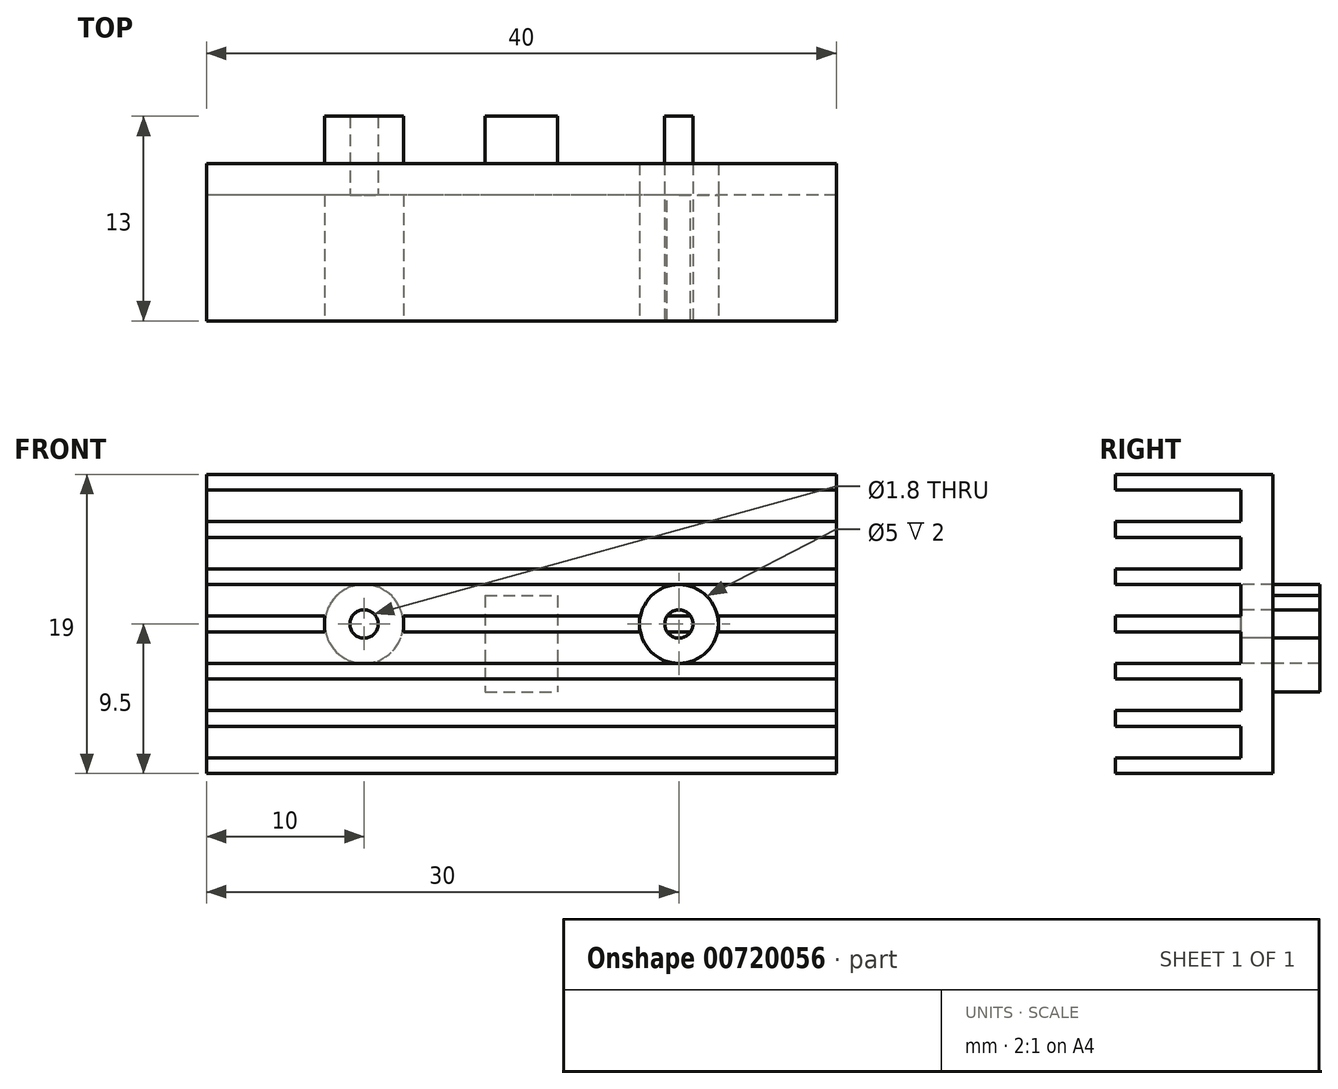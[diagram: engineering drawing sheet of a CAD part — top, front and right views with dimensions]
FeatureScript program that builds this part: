
annotation { "Feature Type Name" : "Feature", "Feature Type Description" : "" }
export const myFeature = defineFeature(function(context is Context, id is Id, definition is map)
    precondition{}
    {
        {
            var Q0;
            Q0=qCreatedBy(makeId("Front.planeOp"),FACE);
            var sketch = newSketch(context, id + "F0", { "sketchPlane" : qUnion([Q0])});
            skLineSegment(sketch, "E0", {"start": v(0, 0) * mm, "end": v(-20, 0) * mm, "construction": true});
            skLineSegment(sketch, "E1", {"start": v(-20, 0) * mm, "end": v(-20, 9.5) * mm, "construction": true});
            skLineSegment(sketch, "E2.bottom", {"start": v(-20, 9.5) * mm, "end": v(20, 9.5) * mm});
            skLineSegment(sketch, "E2.top", {"start": v(-20, -9.5) * mm, "end": v(20, -9.5) * mm});
            skLineSegment(sketch, "E2.left", {"start": v(-20, 9.5) * mm, "end": v(-20, -9.5) * mm});
            skLineSegment(sketch, "E2.right", {"start": v(20, 9.5) * mm, "end": v(20, -9.5) * mm});
            skPoint(sketch, "E2.middle", {"position": v(0, 0) * mm});
            skSolve(sketch);
        }
        {
            var Q0;
            Q0=makeQuery(id+"F0.imprint","IMPRINT",FACE,{"disambiguationData":[TD([[makeQuery(id+"F0.imprint","IMPRINT",EDGE,{"derivedFrom":sQuery(id+"F0.wireOp",EDGE,"E2.bottom")}),-1.0]])]});
            extrude(context, id + "F1", {"entities" : qUnion([Q0]), "depth" : 10 * mm, "offsetDistance" : 25 * mm});
        }
        {
            var Q0;
            Q0=makeQuery(id+"F1.opExtrude","CAP_FACE",FACE,{"disambiguationData":[OSD([sQuery(id+"F0.wireOp",EDGE,"E2.bottom"),sQuery(id+"F0.wireOp",EDGE,"E2.top"),sQuery(id+"F0.wireOp",EDGE,"E2.left"),sQuery(id+"F0.wireOp",EDGE,"E2.right")])],"isStart":false});
            var sketch = newSketch(context, id + "F2", { "sketchPlane" : qUnion([Q0])});
            skLineSegment(sketch, "E3", {"start": v(-20, 0) * mm, "end": v(-20, 0.5) * mm, "construction": true});
            skLineSegment(sketch, "E4.bottom", {"start": v(-20, 0.5) * mm, "end": v(20, 0.5) * mm});
            skLineSegment(sketch, "E4.top", {"start": v(-20, -0.5) * mm, "end": v(20, -0.5) * mm});
            skLineSegment(sketch, "E4.left", {"start": v(-20, 0.5) * mm, "end": v(-20, -0.5) * mm});
            skLineSegment(sketch, "E4.right", {"start": v(20, 0.5) * mm, "end": v(20, -0.5) * mm});
            skPoint(sketch, "E4.middle", {"position": v(0, 0) * mm});
            skLineSegment(sketch, "E5.0.1.0", {"start": v(-20, 3.5) * mm, "end": v(20, 3.5) * mm});
            skLineSegment(sketch, "E5.0.1.1", {"start": v(-20, 3.5) * mm, "end": v(-20, 2.5) * mm});
            skLineSegment(sketch, "E5.0.1.2", {"start": v(-20, 2.5) * mm, "end": v(20, 2.5) * mm});
            skLineSegment(sketch, "E5.0.1.3", {"start": v(20, 3.5) * mm, "end": v(20, 2.5) * mm});
            skLineSegment(sketch, "E5.0.2.0", {"start": v(-20, 6.5) * mm, "end": v(20, 6.5) * mm});
            skLineSegment(sketch, "E5.0.2.1", {"start": v(-20, 6.5) * mm, "end": v(-20, 5.5) * mm});
            skLineSegment(sketch, "E5.0.2.2", {"start": v(-20, 5.5) * mm, "end": v(20, 5.5) * mm});
            skLineSegment(sketch, "E5.0.2.3", {"start": v(20, 6.5) * mm, "end": v(20, 5.5) * mm});
            skLineSegment(sketch, "E5.direction1", {"start": v(-25, 0.5) * mm, "end": v(-20, 0.5) * mm, "construction": true});
            skLineSegment(sketch, "E5.direction2", {"start": v(-20, 0.5) * mm, "end": v(-20, 3.5) * mm, "construction": true});
            skLineSegment(sketch, "E6.0.1.0", {"start": v(-20, -2.5) * mm, "end": v(20, -2.5) * mm});
            skLineSegment(sketch, "E6.0.1.1", {"start": v(-20, -2.5) * mm, "end": v(-20, -3.5) * mm});
            skLineSegment(sketch, "E6.0.1.2", {"start": v(-20, -3.5) * mm, "end": v(20, -3.5) * mm});
            skLineSegment(sketch, "E6.0.1.3", {"start": v(20, -2.5) * mm, "end": v(20, -3.5) * mm});
            skLineSegment(sketch, "E6.0.2.0", {"start": v(-20, -5.5) * mm, "end": v(20, -5.5) * mm});
            skLineSegment(sketch, "E6.0.2.1", {"start": v(-20, -5.5) * mm, "end": v(-20, -6.5) * mm});
            skLineSegment(sketch, "E6.0.2.2", {"start": v(-20, -6.5) * mm, "end": v(20, -6.5) * mm});
            skLineSegment(sketch, "E6.0.2.3", {"start": v(20, -5.5) * mm, "end": v(20, -6.5) * mm});
            skLineSegment(sketch, "E6.direction2", {"start": v(-20, 0.5) * mm, "end": v(-20, -2.5) * mm, "construction": true});
            skLineSegment(sketch, "E7.0.0.3", {"start": v(-20, 9.5) * mm, "end": v(20, 9.5) * mm});
            skLineSegment(sketch, "E7.3.0.3", {"start": v(-20, 9.5) * mm, "end": v(-20, 8.5) * mm});
            skLineSegment(sketch, "E7.6.0.3", {"start": v(-20, 8.5) * mm, "end": v(20, 8.5) * mm});
            skLineSegment(sketch, "E7.9.0.3", {"start": v(20, 9.5) * mm, "end": v(20, 8.5) * mm});
            skLineSegment(sketch, "E8.0.0.3", {"start": v(-20, -8.5) * mm, "end": v(20, -8.5) * mm});
            skLineSegment(sketch, "E8.3.0.3", {"start": v(-20, -8.5) * mm, "end": v(-20, -9.5) * mm});
            skLineSegment(sketch, "E8.6.0.3", {"start": v(-20, -9.5) * mm, "end": v(20, -9.5) * mm});
            skLineSegment(sketch, "E8.9.0.3", {"start": v(20, -8.5) * mm, "end": v(20, -9.5) * mm});
            skSolve(sketch);
        }
        {
            var Q0;
            Q0=qCreatedBy(makeId("Front.planeOp"),FACE);
            cPlane(context, id + "F3", {"entities" : qUnion([Q0]), "cplaneType" : CPlaneType.OFFSET, "offset" : 2 * mm, "width" : 150 * mm, "height" : 150 * mm});
        }
        {
            var Q0;
            {var subQ0=sQuery(id+"F2.wireOp",EDGE,"E5.0.2.0");Q0=makeQuery(id+"F2.imprint","IMPRINT",FACE,{"disambiguationData":[TD([[makeQuery(id+"F2.imprint","IMPRINT",EDGE,{"derivedFrom":subQ0}),1.0]])]});}
            var Q1;
            {var subQ0=sQuery(id+"F2.wireOp",EDGE,"E5.0.1.0");Q1=makeQuery(id+"F2.imprint","IMPRINT",FACE,{"disambiguationData":[TD([[makeQuery(id+"F2.imprint","IMPRINT",EDGE,{"derivedFrom":subQ0}),1.0]])]});}
            var Q2;
            {var subQ0=sQuery(id+"F2.wireOp",EDGE,"E4.bottom");Q2=makeQuery(id+"F2.imprint","IMPRINT",FACE,{"disambiguationData":[TD([[makeQuery(id+"F2.imprint","IMPRINT",EDGE,{"derivedFrom":subQ0}),1.0]])]});}
            var Q3;
            {var subQ0=sQuery(id+"F2.wireOp",EDGE,"E4.top");Q3=makeQuery(id+"F2.imprint","IMPRINT",FACE,{"disambiguationData":[TD([[makeQuery(id+"F2.imprint","IMPRINT",EDGE,{"derivedFrom":subQ0}),-1.0]])]});}
            var Q4;
            {var subQ0=sQuery(id+"F2.wireOp",EDGE,"E6.0.1.2");Q4=makeQuery(id+"F2.imprint","IMPRINT",FACE,{"disambiguationData":[TD([[makeQuery(id+"F2.imprint","IMPRINT",EDGE,{"derivedFrom":subQ0}),-1.0]])]});}
            var Q5;
            {var subQ0=sQuery(id+"F2.wireOp",EDGE,"E6.0.2.2");Q5=makeQuery(id+"F2.imprint","IMPRINT",FACE,{"disambiguationData":[TD([[makeQuery(id+"F2.imprint","IMPRINT",EDGE,{"derivedFrom":subQ0}),-1.0]])]});}
            var Q6;
            Q6=qCreatedBy(id+"F3.planeOp",FACE);
            extrude(context, id + "F4", {"entities" : qUnion([Q0, Q1, Q2, Q3, Q4, Q5]), "operationType" : NewBodyOperationType.REMOVE, "endBound" : BoundingType.UP_TO_SURFACE, "oppositeDirection" : true, "depth" : 25 * mm, "endBoundEntityFace" : qUnion([Q6]), "offsetDistance" : 25 * mm});
        }
        {
            var Q0;
            Q0=qCreatedBy(id+"F3.planeOp",FACE);
            var sketch = newSketch(context, id + "F5", { "sketchPlane" : qUnion([Q0])});
            skLineSegment(sketch, "E9", {"start": v(0, 0) * mm, "end": v(-10, 0) * mm, "construction": true});
            skLineSegment(sketch, "E10", {"start": v(0, 0) * mm, "end": v(-2.3, 0) * mm, "construction": true});
            skLineSegment(sketch, "E11", {"start": v(-2.3, 0) * mm, "end": v(-2.3, 1.8) * mm, "construction": true});
            skLineSegment(sketch, "E12", {"start": v(0, 0) * mm, "end": v(2.3, 0) * mm, "construction": true});
            skLineSegment(sketch, "E13", {"start": v(2.3, 0) * mm, "end": v(2.3, -4.3) * mm, "construction": true});
            skLineSegment(sketch, "E14.bottom", {"start": v(-2.3, 1.8) * mm, "end": v(2.3, 1.8) * mm});
            skLineSegment(sketch, "E14.top", {"start": v(-2.3, -4.3) * mm, "end": v(2.3, -4.3) * mm});
            skLineSegment(sketch, "E14.left", {"start": v(-2.3, 1.8) * mm, "end": v(-2.3, -4.3) * mm});
            skLineSegment(sketch, "E14.right", {"start": v(2.3, 1.8) * mm, "end": v(2.3, -4.3) * mm});
            skCircle(sketch, "E15", {"center": v(-10, 0) * mm, "radius": 0.9 * mm});
            skCircle(sketch, "E16", {"center": v(-10, 0) * mm, "radius": 2.5 * mm});
            skLineSegment(sketch, "E17.bottom", {"start": v(-7.5, 2.5) * mm, "end": v(-12.5, 2.5) * mm});
            skLineSegment(sketch, "E17.top", {"start": v(-7.5, -2.5) * mm, "end": v(-12.5, -2.5) * mm});
            skLineSegment(sketch, "E17.left", {"start": v(-7.5, 2.5) * mm, "end": v(-7.5, -2.5) * mm});
            skLineSegment(sketch, "E17.right", {"start": v(-12.5, 2.5) * mm, "end": v(-12.5, -2.5) * mm});
            skLineSegment(sketch, "E18.MirrorCS", {"start": v(7.5, 2.5) * mm, "end": v(7.5, -2.5) * mm});
            skLineSegment(sketch, "E19.MirrorCS", {"start": v(7.5, 2.5) * mm, "end": v(12.5, 2.5) * mm});
            skCircle(sketch, "E20.MirrorC", {"center": v(10, 0) * mm, "radius": 2.5 * mm});
            skCircle(sketch, "E21.MirrorC", {"center": v(10, 0) * mm, "radius": 0.9 * mm});
            skLineSegment(sketch, "E22.MirrorCS", {"start": v(7.5, -2.5) * mm, "end": v(12.5, -2.5) * mm});
            skLineSegment(sketch, "E23.MirrorCS", {"start": v(12.5, 2.5) * mm, "end": v(12.5, -2.5) * mm});
            skSolve(sketch);
        }
        {
            var Q0;
            Q0=makeQuery(id+"F1.opExtrude","CAP_FACE",FACE,{"disambiguationData":[OSD([sQuery(id+"F0.wireOp",EDGE,"E2.bottom"),sQuery(id+"F0.wireOp",EDGE,"E2.top"),sQuery(id+"F0.wireOp",EDGE,"E2.left"),sQuery(id+"F0.wireOp",EDGE,"E2.right")])],"isStart":true});
            cPlane(context, id + "F6", {"entities" : qUnion([Q0]), "cplaneType" : CPlaneType.OFFSET, "offset" : 3 * mm, "width" : 150 * mm, "height" : 150 * mm});
        }
        {
            var Q0;
            Q0=makeQuery(id+"F5.imprint","IMPRINT",FACE,{"disambiguationData":[TD([[makeQuery(id+"F5.imprint","IMPRINT",EDGE,{"derivedFrom":sQuery(id+"F5.wireOp",EDGE,"vaRRFQnh-6l4D-KlI0-Jkj3-9eLInDPzyhP6")}),-1.0]])]});
            var Q1;
            Q1=makeQuery(id+"F5.imprint","IMPRINT",FACE,{"disambiguationData":[TD([[makeQuery(id+"F5.imprint","IMPRINT",EDGE,{"derivedFrom":sQuery(id+"F5.wireOp",EDGE,"9a7e4fac-4f94-4cee-be25-9ec4bdd4e4ea0.MirrorCS")}),1.0]])]});
            var Q2;
            Q2=makeQuery(id+"F5.imprint","IMPRINT",FACE,{"disambiguationData":[TD([[makeQuery(id+"F5.imprint","IMPRINT",EDGE,{"derivedFrom":sQuery(id+"F5.wireOp",EDGE,"a2d8c586-922a-4cda-b88e-0afdd4da38a10.MirrorC")}),-1.0]])]});
            var Q3;
            Q3=makeQuery(id+"F5.imprint","IMPRINT",FACE,{"disambiguationData":[TD([[makeQuery(id+"F5.imprint","IMPRINT",EDGE,{"derivedFrom":sQuery(id+"F5.wireOp",EDGE,"0d76e255-3535-46df-a2f9-a872d0353cb00.MirrorC")}),1.0]])]});
            var Q4;
            Q4=makeQuery(id+"F5.imprint","IMPRINT",FACE,{"disambiguationData":[TD([[makeQuery(id+"F5.imprint","IMPRINT",EDGE,{"derivedFrom":sQuery(id+"F5.wireOp",EDGE,"E21.MirrorC")}),1.0]])]});
            var Q5;
            Q5=makeQuery(id+"F5.imprint","IMPRINT",FACE,{"disambiguationData":[TD([[makeQuery(id+"F5.imprint","IMPRINT",EDGE,{"derivedFrom":sQuery(id+"F5.wireOp",EDGE,"E15")}),-1.0]])]});
            var Q6;
            Q6=makeQuery(id+"F5.imprint","IMPRINT",FACE,{"disambiguationData":[TD([[makeQuery(id+"F5.imprint","IMPRINT",EDGE,{"derivedFrom":sQuery(id+"F5.wireOp",EDGE,"E14.bottom")}),-1.0]])]});
            var Q7;
            Q7=qCreatedBy(id+"F6.planeOp",FACE);
            extrude(context, id + "F7", {"entities" : qUnion([Q0, Q1, Q2, Q3, Q4, Q5, Q6]), "operationType" : NewBodyOperationType.ADD, "endBound" : BoundingType.UP_TO_SURFACE, "oppositeDirection" : true, "depth" : 25 * mm, "endBoundEntityFace" : qUnion([Q7]), "offsetDistance" : 25 * mm});
        }
        {
            var Q0;
            Q0=makeQuery(id+"F5.imprint","IMPRINT",FACE,{"disambiguationData":[TD([[makeQuery(id+"F5.imprint","IMPRINT",EDGE,{"derivedFrom":sQuery(id+"F5.wireOp",EDGE,"jt35dyTl-ikho-eOT0-DAPU-rAh0OH2Ca2D4")}),-1.0]])]});
            var Q1;
            Q1=makeQuery(id+"F5.imprint","IMPRINT",FACE,{"disambiguationData":[TD([[makeQuery(id+"F5.imprint","IMPRINT",EDGE,{"derivedFrom":sQuery(id+"F5.wireOp",EDGE,"NUw0Rw4t-io0l-YQbQ-xWhD-a46VIXt3r54f")}),-1.0]])]});
            var Q2;
            Q2=makeQuery(id+"F5.imprint","IMPRINT",FACE,{"disambiguationData":[TD([[makeQuery(id+"F5.imprint","IMPRINT",EDGE,{"derivedFrom":sQuery(id+"F5.wireOp",EDGE,"NUw0Rw4t-io0l-YQbQ-xWhD-a46VIXt3r54f")}),1.0]])]});
            var Q3;
            Q3=makeQuery(id+"F5.imprint","IMPRINT",FACE,{"disambiguationData":[TD([[makeQuery(id+"F5.imprint","IMPRINT",EDGE,{"derivedFrom":sQuery(id+"F5.wireOp",EDGE,"03f16da8-e4e8-4d85-aba3-7918eac5e81c.1.0.0")}),1.0]])]});
            var Q4;
            Q4=makeQuery(id+"F5.imprint","IMPRINT",FACE,{"disambiguationData":[TD([[makeQuery(id+"F5.imprint","IMPRINT",EDGE,{"derivedFrom":sQuery(id+"F5.wireOp",EDGE,"03f16da8-e4e8-4d85-aba3-7918eac5e81c.1.0.4")}),1.0]])]});
            var Q5;
            Q5=makeQuery(id+"F5.imprint","IMPRINT",FACE,{"disambiguationData":[TD([[makeQuery(id+"F5.imprint","IMPRINT",EDGE,{"derivedFrom":sQuery(id+"F5.wireOp",EDGE,"03f16da8-e4e8-4d85-aba3-7918eac5e81c.1.0.5")}),1.0]])]});
            var Q6;
            Q6=makeQuery(id+"F5.imprint","IMPRINT",FACE,{"disambiguationData":[TD([[makeQuery(id+"F5.imprint","IMPRINT",EDGE,{"derivedFrom":sQuery(id+"F5.wireOp",EDGE,"03f16da8-e4e8-4d85-aba3-7918eac5e81c.0.1.0")}),1.0]])]});
            var Q7;
            Q7=makeQuery(id+"F5.imprint","IMPRINT",FACE,{"disambiguationData":[TD([[makeQuery(id+"F5.imprint","IMPRINT",EDGE,{"derivedFrom":sQuery(id+"F5.wireOp",EDGE,"03f16da8-e4e8-4d85-aba3-7918eac5e81c.0.1.4")}),1.0]])]});
            var Q8;
            Q8=makeQuery(id+"F5.imprint","IMPRINT",FACE,{"disambiguationData":[TD([[makeQuery(id+"F5.imprint","IMPRINT",EDGE,{"derivedFrom":sQuery(id+"F5.wireOp",EDGE,"03f16da8-e4e8-4d85-aba3-7918eac5e81c.0.1.5")}),1.0]])]});
            var Q9;
            Q9=makeQuery(id+"F5.imprint","IMPRINT",FACE,{"disambiguationData":[TD([[makeQuery(id+"F5.imprint","IMPRINT",EDGE,{"derivedFrom":sQuery(id+"F5.wireOp",EDGE,"03f16da8-e4e8-4d85-aba3-7918eac5e81c.1.1.0")}),1.0]])]});
            var Q10;
            Q10=makeQuery(id+"F5.imprint","IMPRINT",FACE,{"disambiguationData":[TD([[makeQuery(id+"F5.imprint","IMPRINT",EDGE,{"derivedFrom":sQuery(id+"F5.wireOp",EDGE,"03f16da8-e4e8-4d85-aba3-7918eac5e81c.1.1.4")}),1.0]])]});
            var Q11;
            Q11=makeQuery(id+"F5.imprint","IMPRINT",FACE,{"disambiguationData":[TD([[makeQuery(id+"F5.imprint","IMPRINT",EDGE,{"derivedFrom":sQuery(id+"F5.wireOp",EDGE,"03f16da8-e4e8-4d85-aba3-7918eac5e81c.1.1.5")}),1.0]])]});
            var Q12;
            Q12=makeQuery(id+"F5.imprint","IMPRINT",FACE,{"disambiguationData":[TD([[makeQuery(id+"F5.imprint","IMPRINT",EDGE,{"derivedFrom":sQuery(id+"F5.wireOp",EDGE,"ad8dfa2b-27ac-4793-8de9-5985fa3aa7040.MirrorC")}),1.0]])]});
            var Q13;
            Q13=makeQuery(id+"F5.imprint","IMPRINT",FACE,{"disambiguationData":[TD([[makeQuery(id+"F5.imprint","IMPRINT",EDGE,{"derivedFrom":sQuery(id+"F5.wireOp",EDGE,"ad8dfa2b-27ac-4793-8de9-5985fa3aa7040.MirrorC")}),-1.0]])]});
            var Q14;
            Q14=makeQuery(id+"F5.imprint","IMPRINT",FACE,{"disambiguationData":[TD([[makeQuery(id+"F5.imprint","IMPRINT",EDGE,{"derivedFrom":sQuery(id+"F5.wireOp",EDGE,"8f5c5904-3a9c-41bb-bb4c-c44c0577cf6c0.MirrorC")}),-1.0]])]});
            var Q15;
            Q15=makeQuery(id+"F5.imprint","IMPRINT",FACE,{"disambiguationData":[TD([[makeQuery(id+"F5.imprint","IMPRINT",EDGE,{"derivedFrom":sQuery(id+"F5.wireOp",EDGE,"79443795-5f22-4850-96de-6a89882279580.MirrorC")}),1.0]])]});
            var Q16;
            Q16=makeQuery(id+"F5.imprint","IMPRINT",FACE,{"disambiguationData":[TD([[makeQuery(id+"F5.imprint","IMPRINT",EDGE,{"derivedFrom":sQuery(id+"F5.wireOp",EDGE,"79443795-5f22-4850-96de-6a89882279580.MirrorC")}),-1.0]])]});
            var Q17;
            Q17=makeQuery(id+"F5.imprint","IMPRINT",FACE,{"disambiguationData":[TD([[makeQuery(id+"F5.imprint","IMPRINT",EDGE,{"derivedFrom":sQuery(id+"F5.wireOp",EDGE,"115d48f7-b85f-44a2-8c5e-97de7b7ec2c00.MirrorC")}),-1.0]])]});
            var Q18;
            Q18=makeQuery(id+"F5.imprint","IMPRINT",FACE,{"disambiguationData":[TD([[makeQuery(id+"F5.imprint","IMPRINT",EDGE,{"derivedFrom":sQuery(id+"F5.wireOp",EDGE,"4b71248d-8159-4820-aea2-80c2b7ea0b7d0.MirrorC")}),1.0]])]});
            var Q19;
            Q19=makeQuery(id+"F5.imprint","IMPRINT",FACE,{"disambiguationData":[TD([[makeQuery(id+"F5.imprint","IMPRINT",EDGE,{"derivedFrom":sQuery(id+"F5.wireOp",EDGE,"4b71248d-8159-4820-aea2-80c2b7ea0b7d0.MirrorC")}),-1.0]])]});
            var Q20;
            Q20=makeQuery(id+"F5.imprint","IMPRINT",FACE,{"disambiguationData":[TD([[makeQuery(id+"F5.imprint","IMPRINT",EDGE,{"derivedFrom":sQuery(id+"F5.wireOp",EDGE,"2becf76c-0659-440b-acd6-233aa11e40930.MirrorC")}),-1.0]])]});
            var Q21;
            Q21=makeQuery(id+"F5.imprint","IMPRINT",FACE,{"disambiguationData":[TD([[makeQuery(id+"F5.imprint","IMPRINT",EDGE,{"derivedFrom":sQuery(id+"F5.wireOp",EDGE,"404a5a20-5de5-4e40-a993-ef5180606b200.MirrorC")}),1.0]])]});
            var Q22;
            Q22=makeQuery(id+"F5.imprint","IMPRINT",FACE,{"disambiguationData":[TD([[makeQuery(id+"F5.imprint","IMPRINT",EDGE,{"derivedFrom":sQuery(id+"F5.wireOp",EDGE,"404a5a20-5de5-4e40-a993-ef5180606b200.MirrorC")}),-1.0]])]});
            var Q23;
            Q23=makeQuery(id+"F5.imprint","IMPRINT",FACE,{"disambiguationData":[TD([[makeQuery(id+"F5.imprint","IMPRINT",EDGE,{"derivedFrom":sQuery(id+"F5.wireOp",EDGE,"aca2cda7-5277-44f8-8964-53229556d0ad0.MirrorC")}),-1.0]])]});
            var Q24;
            Q24=makeQuery(id+"F5.imprint","IMPRINT",FACE,{"disambiguationData":[TD([[makeQuery(id+"F5.imprint","IMPRINT",EDGE,{"derivedFrom":sQuery(id+"F5.wireOp",EDGE,"E16")}),-1.0]])]});
            var Q25;
            Q25=makeQuery(id+"F5.imprint","IMPRINT",FACE,{"disambiguationData":[TD([[makeQuery(id+"F5.imprint","IMPRINT",EDGE,{"derivedFrom":sQuery(id+"F5.wireOp",EDGE,"E15")}),-1.0]])]});
            var Q26;
            Q26=makeQuery(id+"F5.imprint","IMPRINT",FACE,{"disambiguationData":[TD([[makeQuery(id+"F5.imprint","IMPRINT",EDGE,{"derivedFrom":sQuery(id+"F5.wireOp",EDGE,"E15")}),1.0]])]});
            var Q27;
            Q27=makeQuery(id+"F5.imprint","IMPRINT",FACE,{"disambiguationData":[TD([[makeQuery(id+"F5.imprint","IMPRINT",EDGE,{"derivedFrom":sQuery(id+"F5.wireOp",EDGE,"E18.MirrorCS")}),1.0]])]});
            var Q28;
            Q28=makeQuery(id+"F5.imprint","IMPRINT",FACE,{"disambiguationData":[TD([[makeQuery(id+"F5.imprint","IMPRINT",EDGE,{"derivedFrom":sQuery(id+"F5.wireOp",EDGE,"E20.MirrorC")}),-1.0]])]});
            var Q29;
            Q29=makeQuery(id+"F5.imprint","IMPRINT",FACE,{"disambiguationData":[TD([[makeQuery(id+"F5.imprint","IMPRINT",EDGE,{"derivedFrom":sQuery(id+"F5.wireOp",EDGE,"E21.MirrorC")}),-1.0]])]});
            extrude(context, id + "F8", {"entities" : qUnion([Q0, Q1, Q2, Q3, Q4, Q5, Q6, Q7, Q8, Q9, Q10, Q11, Q12, Q13, Q14, Q15, Q16, Q17, Q18, Q19, Q20, Q21, Q22, Q23, Q24, Q25, Q26, Q27, Q28, Q29]), "operationType" : NewBodyOperationType.REMOVE, "endBound" : BoundingType.THROUGH_ALL, "depth" : 25 * mm, "offsetDistance" : 25 * mm});
        }
        {
            var Q0;
            Q0=makeQuery(id+"F5.imprint","IMPRINT",FACE,{"disambiguationData":[TD([[makeQuery(id+"F5.imprint","IMPRINT",EDGE,{"derivedFrom":sQuery(id+"F5.wireOp",EDGE,"195ad68e-fd7b-40a9-8d6c-3065b521f89b0.MirrorC")}),-1.0]])]});
            var Q1;
            Q1=makeQuery(id+"F5.imprint","IMPRINT",FACE,{"disambiguationData":[TD([[makeQuery(id+"F5.imprint","IMPRINT",EDGE,{"derivedFrom":sQuery(id+"F5.wireOp",EDGE,"E21.MirrorC")}),-1.0]])]});
            var Q2;
            Q2=makeQuery(id+"F5.imprint","IMPRINT",FACE,{"disambiguationData":[TD([[makeQuery(id+"F5.imprint","IMPRINT",EDGE,{"derivedFrom":sQuery(id+"F5.wireOp",EDGE,"E15")}),1.0]])]});
            var Q3;
            Q3=makeQuery(id+"F5.imprint","IMPRINT",FACE,{"disambiguationData":[TD([[makeQuery(id+"F5.imprint","IMPRINT",EDGE,{"derivedFrom":sQuery(id+"F5.wireOp",EDGE,"a2d8c586-922a-4cda-b88e-0afdd4da38a10.MirrorC")}),1.0]])]});
            var Q4;
            Q4=makeQuery(id+"F5.imprint","IMPRINT",FACE,{"disambiguationData":[TD([[makeQuery(id+"F5.imprint","IMPRINT",EDGE,{"derivedFrom":sQuery(id+"F5.wireOp",EDGE,"0d76e255-3535-46df-a2f9-a872d0353cb00.MirrorC")}),-1.0]])]});
            var Q5;
            Q5=makeQuery(id+"F5.imprint","IMPRINT",FACE,{"disambiguationData":[TD([[makeQuery(id+"F5.imprint","IMPRINT",EDGE,{"derivedFrom":sQuery(id+"F5.wireOp",EDGE,"vaRRFQnh-6l4D-KlI0-Jkj3-9eLInDPzyhP6")}),1.0]])]});
            extrude(context, id + "F9", {"entities" : qUnion([Q0, Q1, Q2, Q3, Q4, Q5]), "operationType" : NewBodyOperationType.REMOVE, "endBound" : BoundingType.THROUGH_ALL, "oppositeDirection" : true, "depth" : 25 * mm, "offsetDistance" : 25 * mm});
        }
    });
